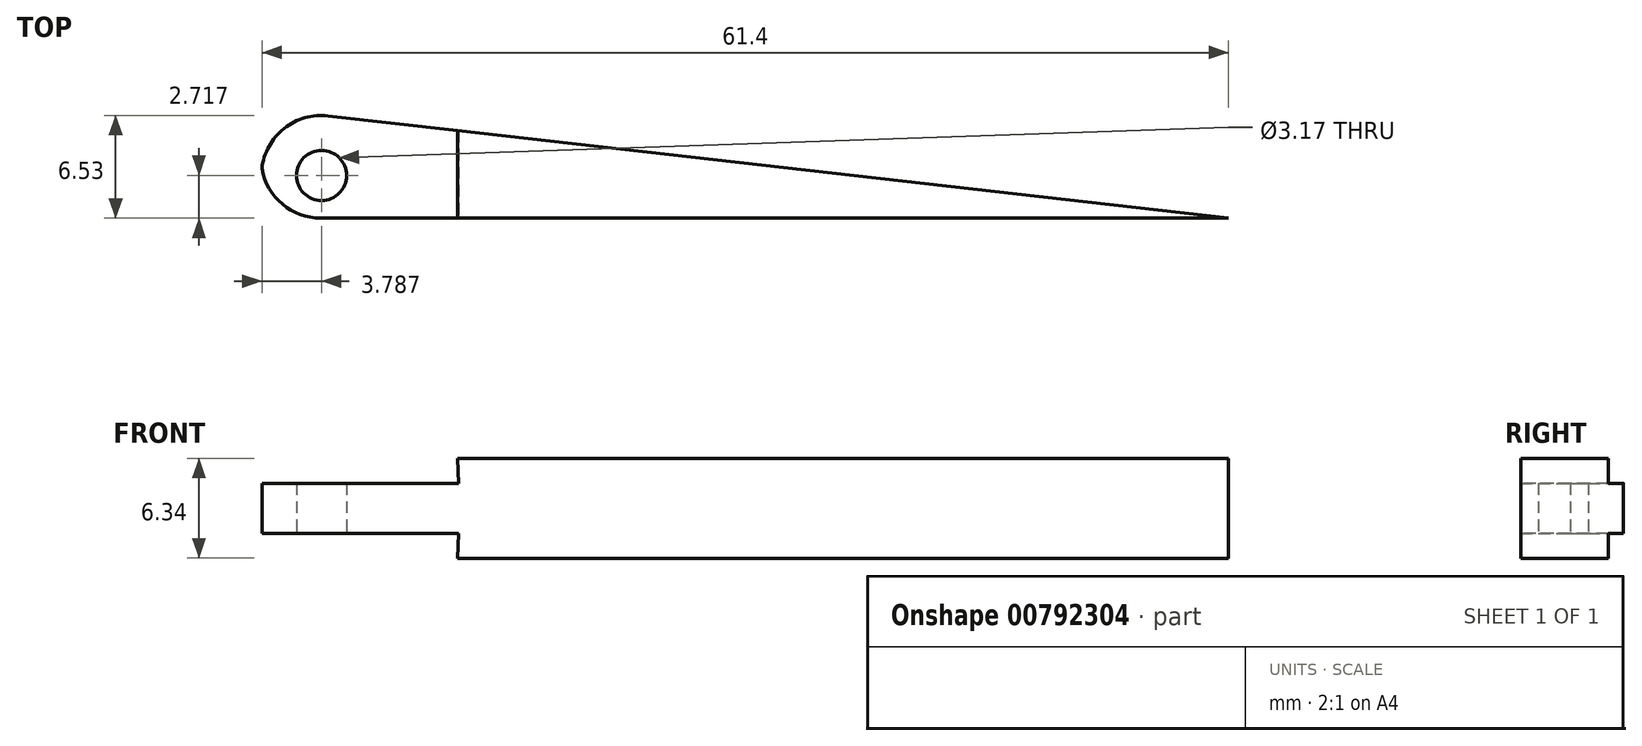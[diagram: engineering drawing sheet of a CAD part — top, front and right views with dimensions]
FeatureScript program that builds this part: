
annotation { "Feature Type Name" : "Feature", "Feature Type Description" : "" }
export const myFeature = defineFeature(function(context is Context, id is Id, definition is map)
    precondition{}
    {
        {
            var Q0;
            Q0=qCreatedBy(makeId("Top.planeOp"),FACE);
            var sketch = newSketch(context, id + "F0", { "sketchPlane" : qUnion([Q0])});
            skLineSegment(sketch, "E0", {"start": v(-31.45, 0) * mm, "end": v(29.9, 0) * mm});
            skLineSegment(sketch, "E1", {"start": v(29.9, 0) * mm, "end": v(-31.67, 7) * mm});
            skLineSegment(sketch, "E2", {"start": v(-31.67, 7) * mm, "end": v(-31.45, 0) * mm});
            skSolve(sketch);
        }
        {
            var Q0;
            Q0=makeQuery(id+"F0.imprint","IMPRINT",FACE,{"disambiguationData":[TD([[makeQuery(id+"F0.imprint","IMPRINT",EDGE,{"derivedFrom":sQuery(id+"F0.wireOp",EDGE,"E0")}),1.0]])]});
            extrude(context, id + "F1", {"entities" : qUnion([Q0]), "endBound" : BoundingType.SYMMETRIC, "depth" : 6.35 * mm, "offsetDistance" : 25.4 * mm});
        }
        {
            var Q0;
            Q0=qCreatedBy(makeId("Front.planeOp"),FACE);
            var sketch = newSketch(context, id + "F2", { "sketchPlane" : qUnion([Q0])});
            skLineSegment(sketch, "E3", {"start": v(-32.35, 1.59) * mm, "end": v(-19.03, 1.59) * mm});
            skLineSegment(sketch, "E4.MirrorCS", {"start": v(-32.35, -1.59) * mm, "end": v(-19.03, -1.59) * mm});
            skLineSegment(sketch, "E5", {"start": v(-19.03, -1.59) * mm, "end": v(-19.03, 1.59) * mm});
            skLineSegment(sketch, "E6", {"start": v(-32.35, -1.59) * mm, "end": v(-32.35, 1.59) * mm});
            skLineSegment(sketch, "E7", {"start": v(-32.35, -1.59) * mm, "end": v(-32.35, -5.3) * mm});
            skLineSegment(sketch, "E8", {"start": v(-32.35, -5.3) * mm, "end": v(-19.12, -5.3) * mm});
            skLineSegment(sketch, "E9", {"start": v(-19.12, -5.3) * mm, "end": v(-19.03, -1.59) * mm});
            skLineSegment(sketch, "E10.MirrorCS", {"start": v(-32.35, 1.59) * mm, "end": v(-32.35, 5.3) * mm});
            skLineSegment(sketch, "E11.MirrorCS", {"start": v(-32.35, 5.3) * mm, "end": v(-19.12, 5.3) * mm});
            skLineSegment(sketch, "E12.MirrorCS", {"start": v(-19.12, 5.3) * mm, "end": v(-19.03, 1.59) * mm});
            skSolve(sketch);
        }
        {
            var Q0;
            Q0=makeQuery(id+"F2.imprint","IMPRINT",FACE,{"disambiguationData":[TD([[makeQuery(id+"F2.imprint","IMPRINT",EDGE,{"derivedFrom":sQuery(id+"F2.wireOp",EDGE,"E3")}),1.0]])]});
            var Q1;
            Q1=makeQuery(id+"F2.imprint","IMPRINT",FACE,{"disambiguationData":[TD([[makeQuery(id+"F2.imprint","IMPRINT",EDGE,{"derivedFrom":sQuery(id+"F2.wireOp",EDGE,"E4.MirrorCS")}),-1.0]])]});
            extrude(context, id + "F3", {"entities" : qUnion([Q0, Q1]), "operationType" : NewBodyOperationType.REMOVE, "oppositeDirection" : true, "depth" : 25.4 * mm, "offsetDistance" : 25.4 * mm});
        }
        {
            var Q0;
            {var subQ0=sQuery(id+"F0.wireOp",EDGE,"E0");var subQ1=sQuery(id+"F0.wireOp",EDGE,"E2");Q0=makeQuery(id+"F3.boolean.opBoolean","SPLIT",EDGE,{"disambiguationData":[TD([makeQuery(id+"F3.opExtrude","SWEPT_FACE",FACE,{"disambiguationData":[OSD([sQuery(id+"F2.wireOp",EDGE,"E4.MirrorCS")])]})])],"derivedFrom":makeQuery(id+"F1.opExtrude","SWEPT_EDGE",EDGE,{"disambiguationData":[OSD([subQ0,subQ1])]})});}
            var Q1;
            {var subQ0=sQuery(id+"F0.wireOp",EDGE,"E0");var subQ1=sQuery(id+"F0.wireOp",EDGE,"E2");Q1=makeQuery(id+"F3.boolean.opBoolean","SPLIT",EDGE,{"disambiguationData":[TD([makeQuery(id+"F3.opExtrude","SWEPT_FACE",FACE,{"disambiguationData":[OSD([sQuery(id+"F2.wireOp",EDGE,"E3")])]})])],"derivedFrom":makeQuery(id+"F1.opExtrude","SWEPT_EDGE",EDGE,{"disambiguationData":[OSD([subQ0,subQ1])]})});}
            var Q2;
            {var subQ0=sQuery(id+"F0.wireOp",EDGE,"E2");var subQ1=sQuery(id+"F0.wireOp",EDGE,"E1");Q2=makeQuery(id+"F3.boolean.opBoolean","SPLIT",EDGE,{"disambiguationData":[TD([makeQuery(id+"F3.opExtrude","SWEPT_FACE",FACE,{"disambiguationData":[OSD([sQuery(id+"F2.wireOp",EDGE,"E3")])]})])],"derivedFrom":makeQuery(id+"F1.opExtrude","SWEPT_EDGE",EDGE,{"disambiguationData":[OSD([subQ1,subQ0])]})});}
            var Q3;
            {var subQ0=sQuery(id+"F0.wireOp",EDGE,"E2");var subQ1=sQuery(id+"F0.wireOp",EDGE,"E1");Q3=makeQuery(id+"F3.boolean.opBoolean","SPLIT",EDGE,{"disambiguationData":[TD([makeQuery(id+"F3.opExtrude","SWEPT_FACE",FACE,{"disambiguationData":[OSD([sQuery(id+"F2.wireOp",EDGE,"E4.MirrorCS")])]})])],"derivedFrom":makeQuery(id+"F1.opExtrude","SWEPT_EDGE",EDGE,{"disambiguationData":[OSD([subQ1,subQ0])]})});}
            fillet(context, id + "F4", {"entities" : qUnion([Q0, Q1, Q2, Q3]), "radius" : 3.8 * mm, "tangentPropagation" : true, "allowEdgeOverflow" : false});
        }
        {
            var Q0;
            Q0=makeQuery(id+"F1.opExtrude","CAP_FACE",FACE,{"disambiguationData":[OSD([sQuery(id+"F0.wireOp",EDGE,"E0"),sQuery(id+"F0.wireOp",EDGE,"E1"),sQuery(id+"F0.wireOp",EDGE,"E2")])],"isStart":true});
            var sketch = newSketch(context, id + "F5", { "sketchPlane" : qUnion([Q0])});
            skPoint(sketch, "E13", {"position": v(-27.72, -2.72) * mm});
            skSolve(sketch);
        }
        {
            var Q0;
            Q0=sQuery(id+"F5.wireOp",VERTEX,"E13");
            var Q1;
            Q1=makeQuery(id+"F1.opExtrude","SWEPT_BODY",BODY,{"disambiguationData":[OSD([sQuery(id+"F0.wireOp",EDGE,"E0"),sQuery(id+"F0.wireOp",EDGE,"E1"),sQuery(id+"F0.wireOp",EDGE,"E2")])]});
            hole(context, id + "F6", {"style" : HoleStyle.SIMPLE, "endStyle" : HoleEndStyle.THROUGH, "holeDiameter" : 3.17 * mm, "majorDiameter" : 6.35 * mm, "isTappedThrough" : true, "tappedDepth" : 12.7 * mm, "tapClearance" : 3, "startFromSketch" : true, "locations" : qUnion([Q0]), "scope" : qUnion([Q1])});
        }
    });
